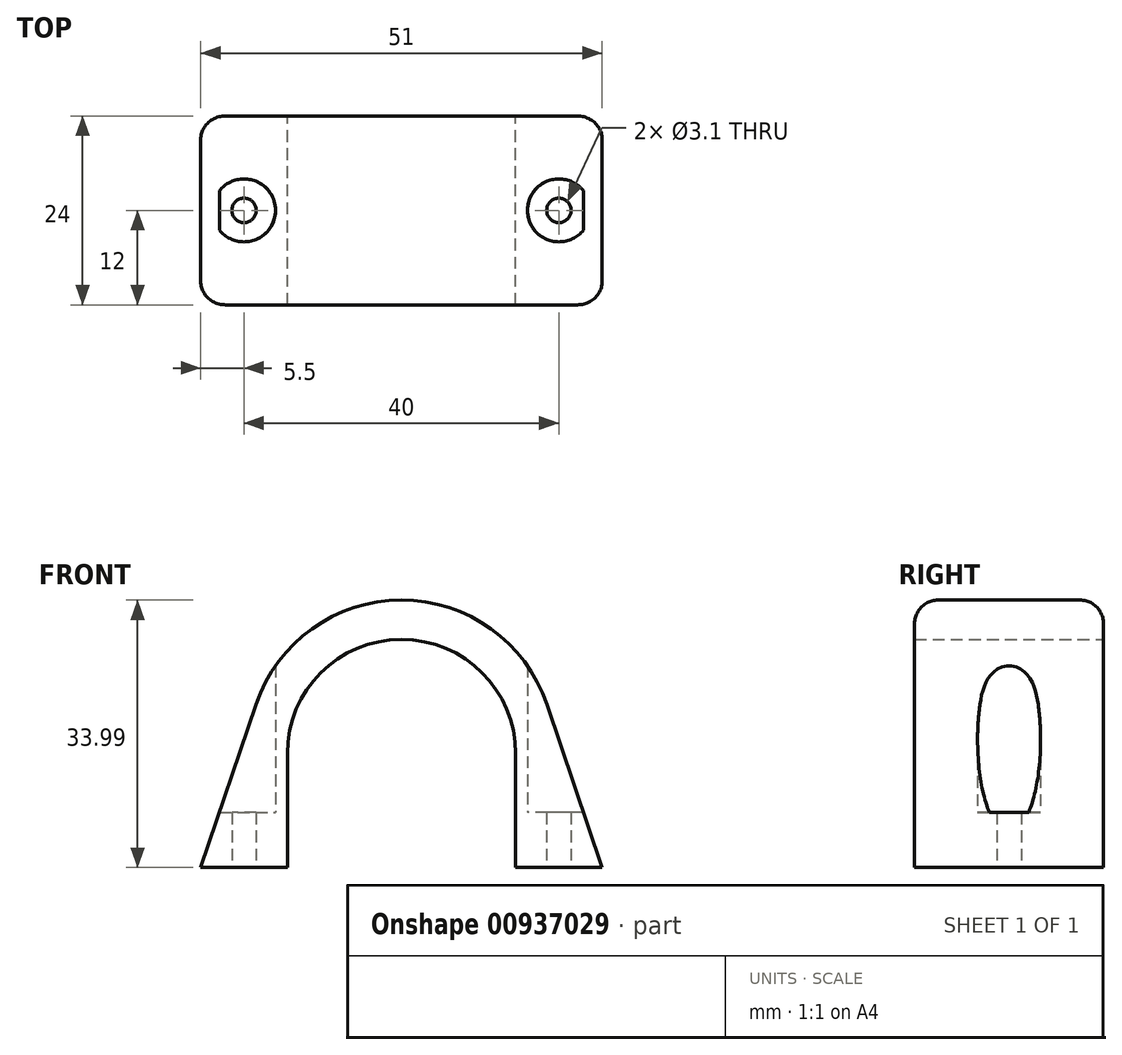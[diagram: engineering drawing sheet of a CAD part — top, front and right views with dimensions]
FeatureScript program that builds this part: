
annotation { "Feature Type Name" : "Feature", "Feature Type Description" : "" }
export const myFeature = defineFeature(function(context is Context, id is Id, definition is map)
    precondition{}
    {
        {
            var Q0;
            Q0=qCreatedBy(makeId("Front.planeOp"),FACE);
            var sketch = newSketch(context, id + "F0", { "sketchPlane" : qUnion([Q0])});
            skLineSegment(sketch, "E0", {"start": v(14.5, 14.49) * mm, "end": v(14.5, 0) * mm});
            skArc(sketch, "E1", {"start": v(14.5, 14.49) * mm, "mid": v(0, 28.99) * mm, "end": v(-14.5, 14.49) * mm});
            skArc(sketch, "E2.0", {"start": v(18.47, 20.75) * mm, "mid": v(0, 33.99) * mm, "end": v(-18.47, 20.75) * mm});
            skLineSegment(sketch, "E3", {"start": v(-18.47, 20.75) * mm, "end": v(-25.5, 0) * mm});
            skLineSegment(sketch, "E4.MirrorCS", {"start": v(18.47, 20.75) * mm, "end": v(25.5, 0) * mm});
            skLineSegment(sketch, "E5", {"start": v(-25.5, 0) * mm, "end": v(-14.5, 0) * mm});
            skLineSegment(sketch, "E6", {"start": v(14.5, 0) * mm, "end": v(25.5, 0) * mm});
            skLineSegment(sketch, "E7", {"start": v(-14.5, 14.49) * mm, "end": v(-14.5, 0) * mm});
            skPoint(sketch, "E8.orphan", {"position": v(-14.5, 0) * mm});
            skSolve(sketch);
        }
        {
            var Q0;
            Q0 = qSketchRegion(id + "F0", true);
            extrude(context, id + "F1", {"entities" : qUnion([Q0]), "depth" : 24 * mm, "offsetDistance" : 25 * mm});
        }
        {
            var Q0;
            Q0=makeQuery(id+"F1.opExtrude","SWEPT_FACE",FACE,{"disambiguationData":[OSD([sQuery(id+"F0.wireOp",EDGE,"E5")])]});
            var sketch = newSketch(context, id + "F2", { "sketchPlane" : qUnion([Q0])});
            skPoint(sketch, "E9", {"position": v(-20, 12) * mm});
            skPoint(sketch, "E10.MirrorP", {"position": v(20, 12) * mm});
            skSolve(sketch);
        }
        {
            var Q0;
            Q0=sQuery(id+"F2.wireOp",VERTEX,"E9");
            var Q1;
            Q1=sQuery(id+"F2.wireOp",VERTEX,"E10.MirrorP");
            var Q2;
            Q2=makeQuery(id+"F1.opExtrude","SWEPT_BODY",BODY,{"disambiguationData":[OSD([sQuery(id+"F0.wireOp",EDGE,"E0"),sQuery(id+"F0.wireOp",EDGE,"E1"),sQuery(id+"F0.wireOp",EDGE,"E2.0"),sQuery(id+"F0.wireOp",EDGE,"E3"),sQuery(id+"F0.wireOp",EDGE,"E4.MirrorCS"),sQuery(id+"F0.wireOp",EDGE,"E5"),sQuery(id+"F0.wireOp",EDGE,"E6"),sQuery(id+"F0.wireOp",EDGE,"E7")])]});
            hole(context, id + "F3", {"style" : HoleStyle.SIMPLE, "endStyle" : HoleEndStyle.THROUGH, "holeDiameter" : 3.1 * mm, "majorDiameter" : 5 * mm, "isTappedThrough" : true, "tappedDepth" : 12 * mm, "tapClearance" : 3, "startFromSketch" : true, "locations" : qUnion([Q0, Q1]), "scope" : qUnion([Q2])});
        }
        {
            var Q0;
            Q0=qCreatedBy(makeId("Top.planeOp"),FACE);
            cPlane(context, id + "F4", {"entities" : qUnion([Q0]), "cplaneType" : CPlaneType.OFFSET, "offset" : 7 * mm, "width" : 150 * mm, "height" : 150 * mm});
        }
        {
            var Q0;
            Q0=qCreatedBy(id+"F4.planeOp",FACE);
            var sketch = newSketch(context, id + "F5", { "sketchPlane" : qUnion([Q0])});
            skPoint(sketch, "E11", {"position": v(-20, -12) * mm});
            skPoint(sketch, "E12.MirrorP", {"position": v(20, -12) * mm});
            skSolve(sketch);
        }
        {
            var Q0;
            Q0=sQuery(id+"F5.wireOp",VERTEX,"E11");
            var Q1;
            Q1=sQuery(id+"F5.wireOp",VERTEX,"E12.MirrorP");
            var Q2;
            Q2=makeQuery(id+"F1.opExtrude","SWEPT_BODY",BODY,{"disambiguationData":[OSD([sQuery(id+"F0.wireOp",EDGE,"E0"),sQuery(id+"F0.wireOp",EDGE,"E1"),sQuery(id+"F0.wireOp",EDGE,"E2.0"),sQuery(id+"F0.wireOp",EDGE,"E3"),sQuery(id+"F0.wireOp",EDGE,"E4.MirrorCS"),sQuery(id+"F0.wireOp",EDGE,"E5"),sQuery(id+"F0.wireOp",EDGE,"E6"),sQuery(id+"F0.wireOp",EDGE,"E7")])]});
            hole(context, id + "F6", {"style" : HoleStyle.SIMPLE, "endStyle" : HoleEndStyle.THROUGH, "oppositeDirection" : true, "holeDiameter" : 8 * mm, "majorDiameter" : 5 * mm, "isTappedThrough" : true, "tappedDepth" : 12 * mm, "tapClearance" : 3, "startFromSketch" : true, "locations" : qUnion([Q0, Q1]), "scope" : qUnion([Q2])});
        }
        {
            var Q0;
            Q0=makeQuery(id+"F1.opExtrude","CAP_EDGE",EDGE,{"disambiguationData":[OSD([sQuery(id+"F0.wireOp",EDGE,"E2.0")])],"isStart":true});
            var Q1;
            Q1=makeQuery(id+"F1.opExtrude","CAP_EDGE",EDGE,{"disambiguationData":[OSD([sQuery(id+"F0.wireOp",EDGE,"E2.0")])],"isStart":false});
            fillet(context, id + "F7", {"entities" : qUnion([Q0, Q1]), "radius" : 3 * mm, "tangentPropagation" : true, "allowEdgeOverflow" : false});
        }
    });
